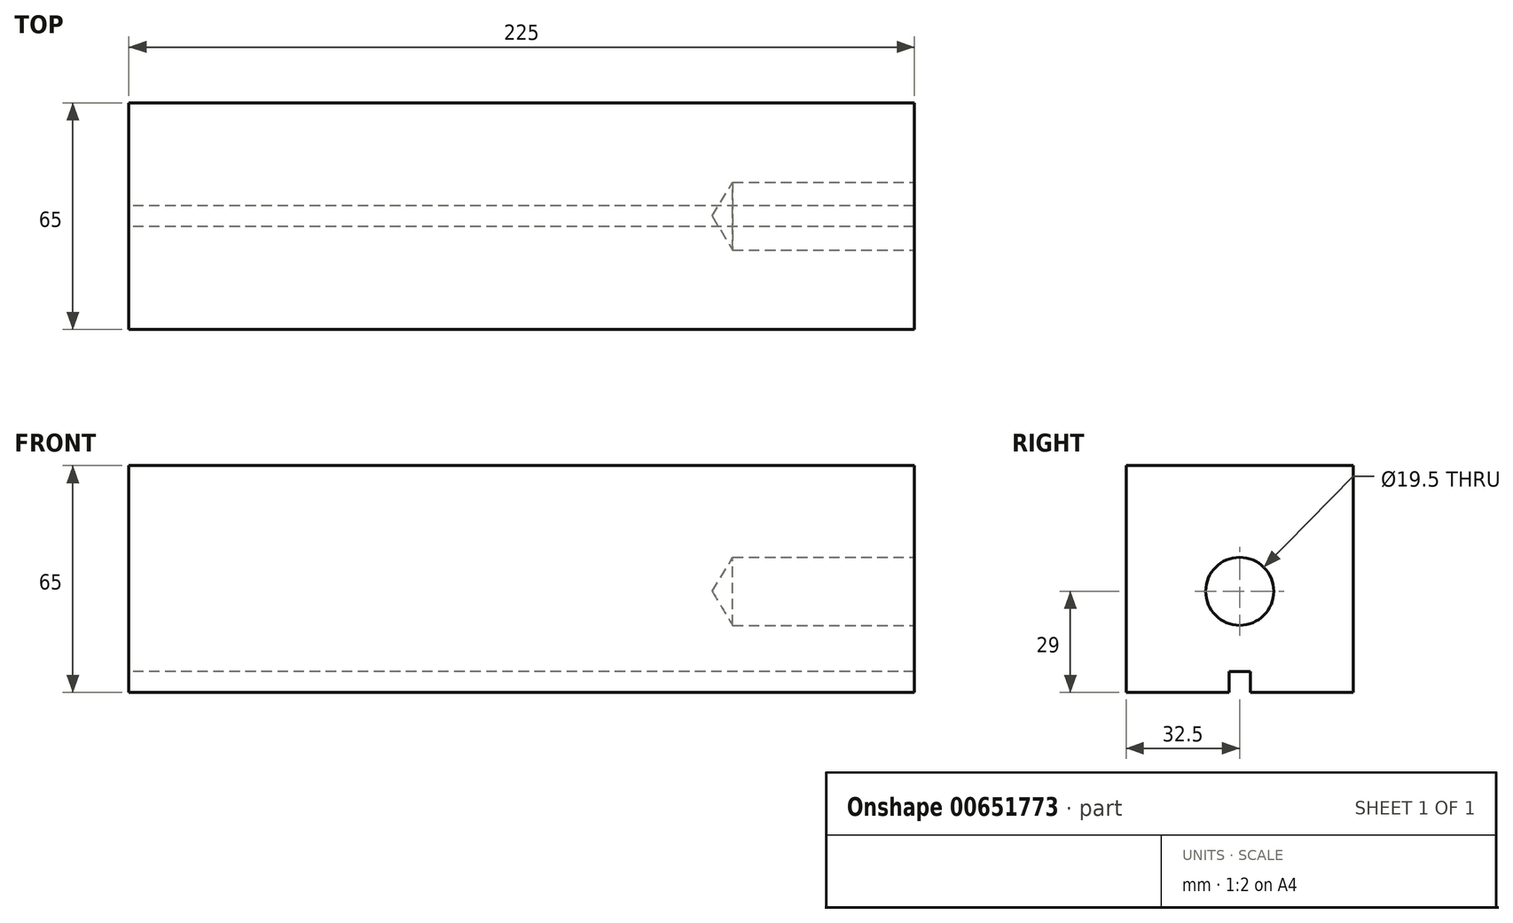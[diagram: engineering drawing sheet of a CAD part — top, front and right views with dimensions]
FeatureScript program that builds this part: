
annotation { "Feature Type Name" : "Feature", "Feature Type Description" : "" }
export const myFeature = defineFeature(function(context is Context, id is Id, definition is map)
    precondition{}
    {
        {
            var Q0;
            Q0=qCreatedBy(makeId("Right.planeOp"),FACE);
            var sketch = newSketch(context, id + "F0", { "sketchPlane" : qUnion([Q0])});
            skLineSegment(sketch, "E0.top", {"start": v(0, 65) * mm, "end": v(32.5, 65) * mm});
            skLineSegment(sketch, "E0.right", {"start": v(32.5, 0) * mm, "end": v(32.5, 65) * mm});
            skLineSegment(sketch, "E1", {"start": v(3, 0) * mm, "end": v(3, 6) * mm});
            skLineSegment(sketch, "E2", {"start": v(3, 6) * mm, "end": v(0, 6) * mm});
            skLineSegment(sketch, "E3", {"start": v(3, 0) * mm, "end": v(32.5, 0) * mm});
            skLineSegment(sketch, "E4", {"start": v(0, 6) * mm, "end": v(0, 65) * mm});
            skSolve(sketch);
        }
        {
            var Q0;
            Q0=makeQuery(id+"F0.imprint","IMPRINT",FACE,{"disambiguationData":[TD([[makeQuery(id+"F0.imprint","IMPRINT",EDGE,{"derivedFrom":sQuery(id+"F0.wireOp",EDGE,"E0.top")}),-1.0]])]});
            extrude(context, id + "F1", {"entities" : qUnion([Q0]), "depth" : 225 * mm, "offsetDistance" : 25 * mm});
        }
        {
            var Q0;
            Q0=makeQuery(id+"F1.opExtrude","CAP_FACE",FACE,{"disambiguationData":[OSD([sQuery(id+"F0.wireOp",EDGE,"E0.top"),sQuery(id+"F0.wireOp",EDGE,"E0.right"),sQuery(id+"F0.wireOp",EDGE,"E1"),sQuery(id+"F0.wireOp",EDGE,"E2"),sQuery(id+"F0.wireOp",EDGE,"E3"),sQuery(id+"F0.wireOp",EDGE,"E4")])],"isStart":false});
            var sketch = newSketch(context, id + "F2", { "sketchPlane" : qUnion([Q0])});
            skArc(sketch, "E5", {"start": v(0, 19.5) * mm, "mid": v(9.5, 29) * mm, "end": v(0, 38.5) * mm});
            skPoint(sketch, "E6", {"position": v(0, 38.5) * mm});
            skPoint(sketch, "E7", {"position": v(0, 19.5) * mm});
            skPoint(sketch, "E8", {"position": v(0, 0) * mm});
            skSolve(sketch);
        }
        {
            var Q0;
            Q0=sQuery(id+"F2.wireOp",VERTEX,"E5.center");
            var Q1;
            Q1=makeQuery(id+"F1.opExtrude","SWEPT_BODY",BODY,{"disambiguationData":[OSD([sQuery(id+"F0.wireOp",EDGE,"E0.top"),sQuery(id+"F0.wireOp",EDGE,"E0.right"),sQuery(id+"F0.wireOp",EDGE,"E1"),sQuery(id+"F0.wireOp",EDGE,"E2"),sQuery(id+"F0.wireOp",EDGE,"E3"),sQuery(id+"F0.wireOp",EDGE,"E4")])]});
            hole(context, id + "F3", {"style" : HoleStyle.SIMPLE, "endStyle" : HoleEndStyle.BLIND, "holeDiameter" : 19.5 * mm, "majorDiameter" : 5 * mm, "holeDepth" : 52 * mm, "isTappedThrough" : true, "tappedDepth" : 12 * mm, "tapClearance" : 3, "locations" : qUnion([Q0]), "scope" : qUnion([Q1])});
        }
        {
            var Q0;
            Q0=makeQuery(id+"F1.opExtrude","SWEPT_BODY",BODY,{"disambiguationData":[OSD([sQuery(id+"F0.wireOp",EDGE,"E0.top"),sQuery(id+"F0.wireOp",EDGE,"E0.right"),sQuery(id+"F0.wireOp",EDGE,"E1"),sQuery(id+"F0.wireOp",EDGE,"E2"),sQuery(id+"F0.wireOp",EDGE,"E3"),sQuery(id+"F0.wireOp",EDGE,"E4")])]});
            var Q1;
            Q1=makeQuery(id+"F1.opExtrude","SWEPT_FACE",FACE,{"disambiguationData":[OSD([sQuery(id+"F0.wireOp",EDGE,"E4")])]});
            mirror(context, id + "F4", {"operationType" : NewBodyOperationType.ADD, "entities" : qUnion([Q0]), "mirrorPlane" : qUnion([Q1])});
        }
    });
